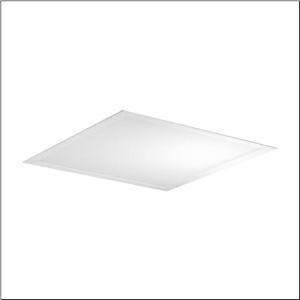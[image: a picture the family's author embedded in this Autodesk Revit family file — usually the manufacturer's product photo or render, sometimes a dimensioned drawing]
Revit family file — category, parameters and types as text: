
# Revit family: apollon_r__31_square_51mp11wd2442m_0a3c
name_source: partatom
category: Lighting Fixtures
units: mm (PartAtom-declared; Revit-internal decimal feet)

## family parameters
Cut with Voids When Loaded = No
Host = Face
Light Source = No
Part Type = Normal
Room Calculation Point = No
Round Connector Dimension = Use Diameter
Shared = No

## types (1)
- Apollon® 31 square (1 x LED, 4000 lm, 27.5 W, 4000K)
    Apparent Load = 28 VA
    CIE Flux Codes = 61 87 97 100 100
    Color Rendering = 80
    Color Temperature = 4000K
    Default Elevation = 1800 mm
    Description = Apollon® 31 square, office luminaire, primary optical cover: micro prismatic cover, of PMMA, CAT 2 (L<= 3000cd/m²), light emission: direct distribution, primary light characteristic: symmetric, installation type: lay-in mounting, LED, rated luminous flux: 4.000lm, luminous efficacy: 145lm/W, light colour: 840, colour temperature: 4000K, with terminal, 5-pole, mains connection: 220..240V, AC/DC, 0/50..60Hz, rated input power: 28W, housing, of aluminium, traffic white (RAL 9016), module: M625, length: 620mm, width: 620mm, height: 32mm, housing upper side, of sheet steel, galvanised, protection rating (complete): IP20, protection rating (on room side): IP40, insulation class (complete): insulation class II (safety insulation), certification: CE, ENEC, impact resistance: IK03, permissible operating ambient temperature: -20..+40°C, permissible storage temperature: -20..+60°C, packaging unit: set of 6
    Height = 0 mm  [stored 0 ft]
    Lamp = 1 x LED
    Lamp Light Flux = 4000 lm
    Lamp Power = 27.5 W
    Lamp count = 1
    Length = 620 mm
    Luminous efficacy = 145 lm/W
    Manufacturer = Siteco
    ModVariant = No
    Model = 51MP11WD2442M
    Mounting Place = Ceiling
    Mounting Type = Recessed
    Number of Poles = 1
    OnlyDefault = Yes
    Power Factor = 1
    Product Name = Apollon® 31 square
    Product group = office luminaire | ceiling recessed
    ProductGroupID = 401
    Protection Class = Protection class II
    Protection Degree = IP 20
    RLX_Detail_Level = 1
    RLX_Emergency_Light_Flux = 0 lm
    RLX_Emergency_Type = 0
    RLX_Emergency_Type_DB = No
    RlxData = <blob elided: 12941 chars, md5=4e2035f2>
    Socket = socket
    Standby Power = 0 W
    System Light Flux = 4000 lm
    System Power = 28 W
    Type Comments = Product without accessories
    Type Image = l_1291039.jpg
    URL = http://relux.com
    VarID = ---
    Voltage = 0 V
    Weight = 0.00 kg
    Width = 620 mm

note: [stored X ft] marks values corroborated as IEEE doubles in the binary element streams (Revit-internal decimal feet)

## geometry (parser evidence)
native form markers: Sweep x9
no freeform markers — native parametric forms only
